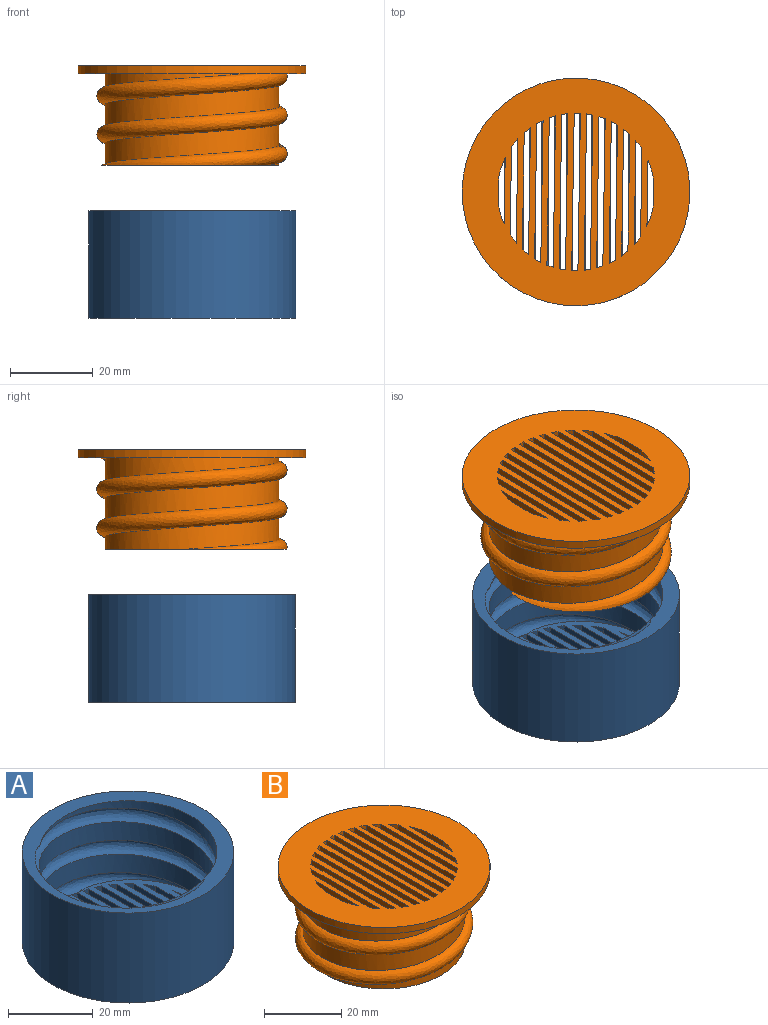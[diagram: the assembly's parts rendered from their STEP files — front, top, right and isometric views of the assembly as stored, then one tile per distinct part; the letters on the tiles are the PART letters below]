
ASSEMBLY  parts=2 mates=1
PART A: 48 faces, bbox 50.6x50.6x30.6 mm
  f0: plane 41.4x19.25mm, normal (0,0,1), area 331.4mm2, adj f10,f13,f14,f23,f32,f33,f34,f35
  f1: plane 41.97x1.5mm, normal (0,0,1), area 62.8mm2, adj f10,f15,f30
  f2: plane 41.33x1.5mm, normal (0,0,1), area 61.5mm2, adj f10,f29,f31
  f3: plane 39.77x1.5mm, normal (0,0,1), area 58.8mm2, adj f10,f27,f28
  f4: plane 37.2x1.5mm, normal (0,0,1), area 54.5mm2, adj f10,f25,f26
  f5: plane 18.91x1.5mm, normal (0,0,1), area 23.1mm2, adj f10,f19,f21
  f6: plane 27.78x1.5mm, normal (0,0,1), area 38.9mm2, adj f10,f17,f20
  f7: plane 33.37x1.5mm, normal (0,0,1), area 48.2mm2, adj f10,f18,f24
  f8: plane 41.97x1.5mm, normal (0,0,1), area 62.8mm2, adj f10,f16,f22
  f9: plane 50x50mm, normal (0,0,-1), area 1274mm2, adj f10,f11,f15,f16,f17,f18,f19,f20
  f10: cylinder r=21mm len=42mm, axis (0,0,-1), area 1960.1mm2, adj f0,f1,f2,f3,f4,f5,f6,f7
  f11: cylinder r=25mm len=50mm, axis (0,0,-1), area 4084.1mm2, adj f9,f12
  f12: plane 50x50mm, normal (0,0,1), area 485.4mm2, adj f10,f11,f14
  f13: plane 2.57x2.56mm, normal (0,1,0.07), area 3.1mm2, adj f0,f10,f14
  f14: bspline ~45.96x45.91mm, area 2206.7mm2, adj f0,f10,f12,f13
  f15: plane 41.97x2mm, normal (1,0,0), area 83.9mm2, adj f1,f9,f10
  f16: plane 41.97x2mm, normal (-1,0,0), area 83.9mm2, adj f8,f9,f10
  f17: plane 27.78x2mm, normal (1,0,0), area 55.6mm2, adj f6,f9,f10
  f18: plane 30.85x2mm, normal (-1,0,0), area 61.7mm2, adj f7,f9,f10
  f19: plane 18.91x2mm, normal (1,0,0), area 37.8mm2, adj f5,f9,f10
  f20: plane 23.95x2mm, normal (-1,0,0), area 47.9mm2, adj f6,f9,f10
  f21: plane 11.12x2mm, normal (-1,0,0), area 22.2mm2, adj f5,f9,f10
  f22: plane 41.76x2mm, normal (1,0,0), area 83.5mm2, adj f8,f9,f10
  f23: plane 41.33x2mm, normal (-1,0,0), area 82.6mm2, adj f0,f9,f10
  f24: plane 33.37x2mm, normal (1,0,0), area 66.7mm2, adj f7,f9,f10
  f25: plane 35.46x2mm, normal (-1,0,0), area 70.9mm2, adj f4,f9,f10
  f26: plane 37.2x2mm, normal (1,0,0), area 74.4mm2, adj f4,f9,f10
  f27: plane 38.62x2mm, normal (-1,0,0), area 77.2mm2, adj f3,f9,f10
  f28: plane 39.77x2mm, normal (1,0,0), area 79.5mm2, adj f3,f9,f10
  f29: plane 40.67x2mm, normal (-1,0,0), area 81.3mm2, adj f2,f9,f10
  f30: plane 41.76x2mm, normal (-1,0,0), area 83.5mm2, adj f1,f9,f10
  f31: plane 41.33x2mm, normal (1,0,0), area 82.6mm2, adj f2,f9,f10
  f32: cylinder r=21mm len=2mm, axis (0,0,-1), area 3.3mm2, adj f0,f9,f33,f34
  f33: plane 37.2x2mm, normal (-1,0,0), area 74.4mm2, adj f0,f9,f10,f32
  f34: plane 38.62x2mm, normal (1,0,0), area 77.2mm2, adj f0,f9,f10,f32
  f35: cylinder r=21mm len=2mm, axis (0,0,-1), area 3.1mm2, adj f0,f9,f36,f37
  f36: plane 39.77x2mm, normal (-1,0,0), area 79.5mm2, adj f0,f9,f10,f35
  f37: plane 40.67x2mm, normal (1,0,0), area 81.3mm2, adj f0,f9,f10,f35
  f38: cylinder r=21mm len=2mm, axis (0,0,-1), area 3.7mm2, adj f0,f9,f39,f40
  f39: plane 33.37x2mm, normal (-1,0,0), area 66.7mm2, adj f0,f9,f10,f38
  f40: plane 35.46x2mm, normal (1,0,0), area 70.9mm2, adj f0,f9,f10,f38
  f41: cylinder r=21mm len=2mm, axis (0,0,-1), area 4.3mm2, adj f0,f9,f42,f43
  f42: plane 27.78x2mm, normal (-1,0,0), area 55.6mm2, adj f0,f9,f10,f41
  f43: plane 30.85x2mm, normal (1,0,0), area 61.7mm2, adj f0,f9,f10,f41
  f44: cylinder r=21mm len=2.52mm, axis (0,0,-1), area 5.9mm2, adj f0,f9,f45,f46
  f45: plane 18.91x2mm, normal (-1,0,0), area 37.8mm2, adj f0,f9,f10,f44
  f46: plane 23.95x2mm, normal (1,0,0), area 47.9mm2, adj f0,f9,f10,f44
  f47: plane 11.12x2mm, normal (1,0,0), area 22.2mm2, adj f0,f9,f10
PART B: 61 faces, bbox 55x55x30 mm
  f0: plane 39x39mm, normal (0,0,-1), area 622.9mm2, adj f8,f9,f10,f11,f12,f13,f14,f15
  f1: plane 55x55mm, normal (0,0,1), area 1804.2mm2, adj f7,f9,f10,f11,f12,f13,f14,f15
  f2: cylinder r=21mm len=42mm, axis (0,0,-1), area 1662.5mm2, adj f3,f4,f5,f6
  f3: bspline ~45.96x45.91mm, area 2085.8mm2, adj f2,f4,f5,f6
  f4: plane 0.65x0.14mm, normal (0,-1,-0.07), area 0mm2, adj f2,f3,f5
  f5: plane 43.96x42.86mm, normal (0,0,-1), area 283mm2, adj f2,f3,f4,f8
  f6: plane 55x55mm, normal (0,0,-1), area 897.7mm2, adj f2,f3,f7
  f7: cylinder r=27.5mm len=55mm, axis (0,0,-1), area 345.6mm2, adj f1,f6
  f8: cylinder r=19.5mm len=39mm, axis (0,0,-1), area 2707.7mm2, adj f0,f5
  f9: plane 6.14x2mm, normal (-1,0,0), area 12.3mm2, adj f0,f1,f10,f11
  f10: cylinder r=19mm len=4.89mm, axis (0,0,1), area 10.3mm2, adj f0,f1,f9,f12
  f11: cylinder r=19mm len=4.89mm, axis (0,0,1), area 10.3mm2, adj f0,f1,f9,f12
  f12: plane 15.93x2mm, normal (1,0,0), area 31.9mm2, adj f0,f1,f10,f11
  f13: plane 21.25x2mm, normal (-1,0,0), area 42.5mm2, adj f0,f1,f14,f15
  f14: cylinder r=19mm len=2mm, axis (0,0,1), area 4.9mm2, adj f0,f1,f13,f16
  f15: cylinder r=19mm len=2mm, axis (0,0,1), area 4.9mm2, adj f0,f1,f13,f16
  f16: plane 25.13x2mm, normal (1,0,0), area 50.3mm2, adj f0,f1,f14,f15
  f17: plane 28.17x2mm, normal (-1,0,0), area 56.3mm2, adj f0,f1,f18,f19
  f18: cylinder r=19mm len=2mm, axis (0,0,1), area 3.9mm2, adj f0,f1,f17,f20
  f19: cylinder r=19mm len=2mm, axis (0,0,1), area 3.9mm2, adj f0,f1,f17,f20
  f20: plane 30.62x2mm, normal (1,0,0), area 61.2mm2, adj f0,f1,f18,f19
  f21: plane 32.62x2mm, normal (-1,0,0), area 65.2mm2, adj f0,f1,f22,f23
  f22: cylinder r=19mm len=2mm, axis (0,0,1), area 3.4mm2, adj f0,f1,f21,f24
  f23: cylinder r=19mm len=2mm, axis (0,0,1), area 3.4mm2, adj f0,f1,f21,f24
  f24: plane 34.23x2mm, normal (1,0,0), area 68.5mm2, adj f0,f1,f22,f23
  f25: plane 35.52x2mm, normal (-1,0,0), area 71mm2, adj f0,f1,f26,f27
  f26: cylinder r=19mm len=2mm, axis (0,0,1), area 3.2mm2, adj f0,f1,f25,f28
  f27: cylinder r=19mm len=2mm, axis (0,0,1), area 3.2mm2, adj f0,f1,f25,f28
  f28: plane 36.52x2mm, normal (1,0,0), area 73mm2, adj f0,f1,f26,f27
  f29: plane 37.73x2mm, normal (1,0,0), area 75.5mm2, adj f0,f1,f30,f32
  f30: cylinder r=19mm len=2mm, axis (0,0,1), area 3mm2, adj f0,f1,f29,f31
  f31: plane 37.25x2mm, normal (-1,0,0), area 74.5mm2, adj f0,f1,f30,f32
  f32: cylinder r=19mm len=2mm, axis (0,0,1), area 3mm2, adj f0,f1,f29,f31
  f33: plane 37.97x2mm, normal (1,0,0), area 75.9mm2, adj f0,f1,f34,f36
  f34: cylinder r=19mm len=2mm, axis (0,0,1), area 3mm2, adj f0,f1,f33,f35
  f35: plane 37.97x2mm, normal (-1,0,0), area 75.9mm2, adj f0,f1,f34,f36
  f36: cylinder r=19mm len=2mm, axis (0,0,1), area 3mm2, adj f0,f1,f33,f35
  f37: plane 37.73x2mm, normal (-1,0,0), area 75.5mm2, adj f0,f1,f38,f39
  f38: cylinder r=19mm len=2mm, axis (0,0,1), area 3mm2, adj f0,f1,f37,f40
  f39: cylinder r=19mm len=2mm, axis (0,0,1), area 3mm2, adj f0,f1,f37,f40
  f40: plane 37.25x2mm, normal (1,0,0), area 74.5mm2, adj f0,f1,f38,f39
  f41: plane 35.52x2mm, normal (1,0,0), area 71mm2, adj f0,f1,f42,f44
  f42: cylinder r=19mm len=2mm, axis (0,0,1), area 3.2mm2, adj f0,f1,f41,f43
  f43: plane 36.52x2mm, normal (-1,0,0), area 73mm2, adj f0,f1,f42,f44
  f44: cylinder r=19mm len=2mm, axis (0,0,1), area 3.2mm2, adj f0,f1,f41,f43
  f45: plane 32.62x2mm, normal (1,0,0), area 65.2mm2, adj f0,f1,f46,f48
  f46: cylinder r=19mm len=2mm, axis (0,0,1), area 3.4mm2, adj f0,f1,f45,f47
  f47: plane 34.23x2mm, normal (-1,0,0), area 68.5mm2, adj f0,f1,f46,f48
  f48: cylinder r=19mm len=2mm, axis (0,0,1), area 3.4mm2, adj f0,f1,f45,f47
  f49: plane 28.17x2mm, normal (1,0,0), area 56.3mm2, adj f0,f1,f50,f52
  f50: cylinder r=19mm len=2mm, axis (0,0,1), area 3.9mm2, adj f0,f1,f49,f51
  f51: plane 30.62x2mm, normal (-1,0,0), area 61.2mm2, adj f0,f1,f50,f52
  f52: cylinder r=19mm len=2mm, axis (0,0,1), area 3.9mm2, adj f0,f1,f49,f51
  f53: plane 21.25x2mm, normal (1,0,0), area 42.5mm2, adj f0,f1,f54,f56
  f54: cylinder r=19mm len=2mm, axis (0,0,1), area 4.9mm2, adj f0,f1,f53,f55
  f55: plane 25.13x2mm, normal (-1,0,0), area 50.3mm2, adj f0,f1,f54,f56
  f56: cylinder r=19mm len=2mm, axis (0,0,1), area 4.9mm2, adj f0,f1,f53,f55
  f57: plane 6.14x2mm, normal (1,0,0), area 12.3mm2, adj f0,f1,f58,f60
  f58: cylinder r=19mm len=4.89mm, axis (0,0,1), area 10.3mm2, adj f0,f1,f57,f59
  f59: plane 15.93x2mm, normal (-1,0,0), area 31.9mm2, adj f0,f1,f58,f60
  f60: cylinder r=19mm len=4.89mm, axis (0,0,1), area 10.3mm2, adj f0,f1,f57,f59
PLACE A t=(0.73,0,0)mm fixed
PLACE B rot(axis=(0,0,1),179.1deg) t=(0.73,0,33.08)mm
MATE cylindrical B.f7 <-> A.f11  axis (0,0,1) through (0.73,0,59.08)mm
